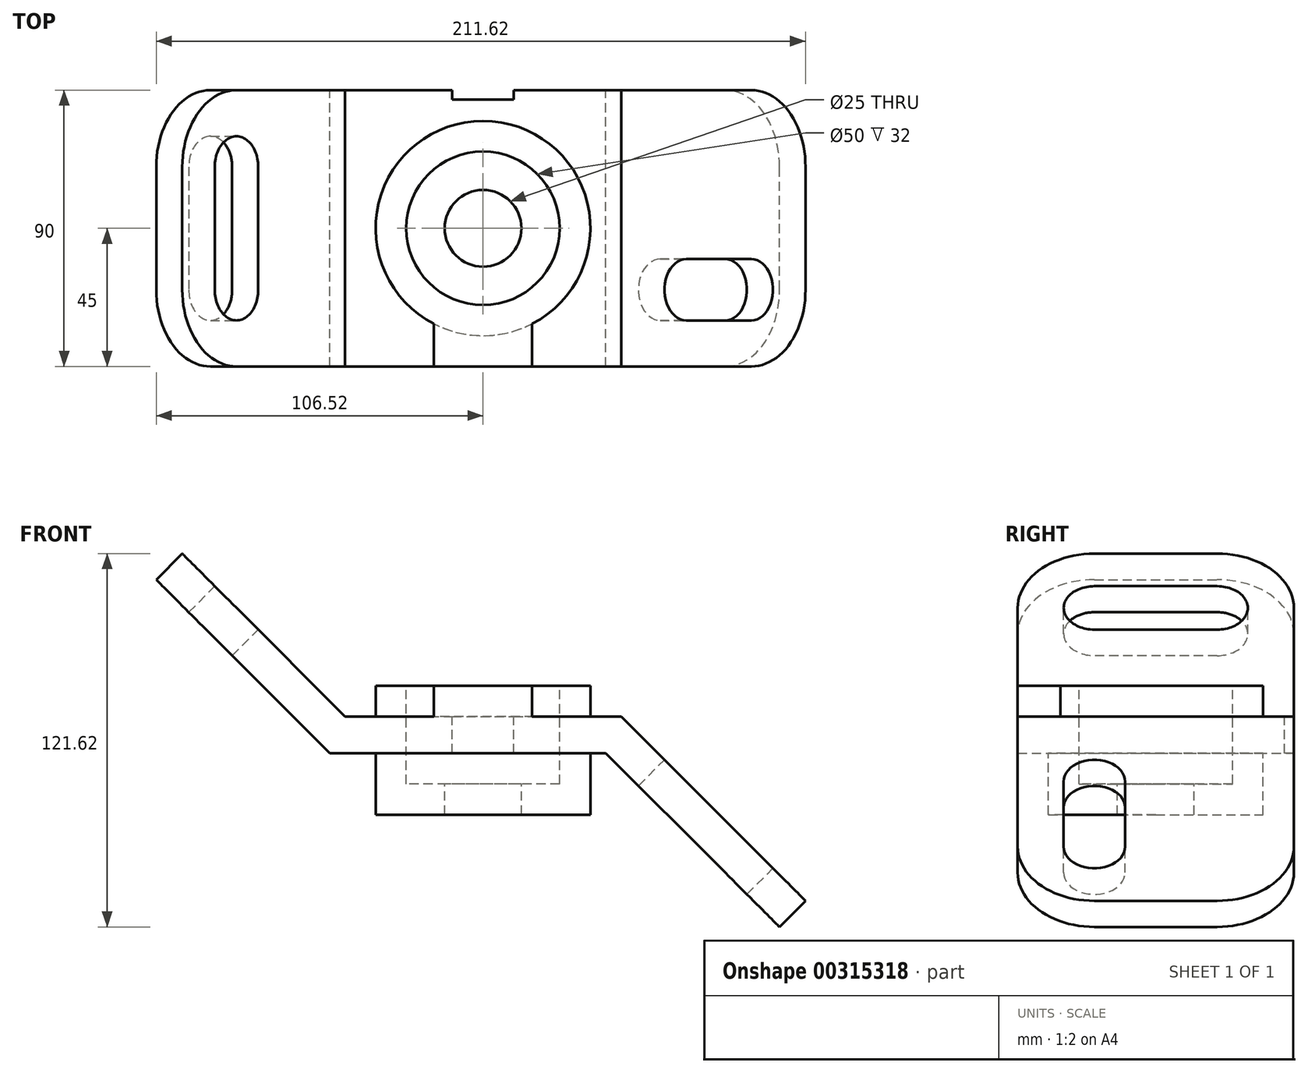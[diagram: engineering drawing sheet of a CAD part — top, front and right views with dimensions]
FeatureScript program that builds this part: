
annotation { "Feature Type Name" : "Feature", "Feature Type Description" : "" }
export const myFeature = defineFeature(function(context is Context, id is Id, definition is map)
    precondition{}
    {
        {
            var Q0;
            Q0=qCreatedBy(makeId("Front.planeOp"),FACE);
            var sketch = newSketch(context, id + "F0", { "sketchPlane" : qUnion([Q0])});
            skLineSegment(sketch, "E0", {"start": v(-98.03, 53.03) * mm, "end": v(-45, 0) * mm});
            skLineSegment(sketch, "E1", {"start": v(-45, 0) * mm, "end": v(45, 0) * mm});
            skLineSegment(sketch, "E2", {"start": v(45, 0) * mm, "end": v(105.1, -60.1) * mm});
            skPoint(sketch, "E3", {"position": v(0, 0) * mm});
            skLineSegment(sketch, "E4.0", {"start": v(40.03, -12) * mm, "end": v(96.62, -68.59) * mm});
            skLineSegment(sketch, "E4.1", {"start": v(-49.97, -12) * mm, "end": v(40.03, -12) * mm});
            skLineSegment(sketch, "E4.2", {"start": v(-106.52, 44.55) * mm, "end": v(-49.97, -12) * mm});
            skLineSegment(sketch, "E5", {"start": v(-106.52, 44.55) * mm, "end": v(-98.03, 53.03) * mm});
            skLineSegment(sketch, "E6", {"start": v(96.62, -68.59) * mm, "end": v(105.1, -60.1) * mm});
            skSolve(sketch);
        }
        {
            var Q0;
            Q0=makeQuery(id+"F0.imprint","IMPRINT",FACE,{"disambiguationData":[TD([[makeQuery(id+"F0.imprint","IMPRINT",EDGE,{"derivedFrom":sQuery(id+"F0.wireOp",EDGE,"E0")}),-1.0]])]});
            extrude(context, id + "F1", {"entities" : qUnion([Q0]), "endBound" : BoundingType.SYMMETRIC, "depth" : 90 * mm});
        }
        {
            var Q0;
            Q0=makeQuery(id+"F1.opExtrude","SWEPT_FACE",FACE,{"disambiguationData":[OSD([sQuery(id+"F0.wireOp",EDGE,"E1")])]});
            var sketch = newSketch(context, id + "F2", { "sketchPlane" : qUnion([Q0])});
            skCircle(sketch, "E7", {"center": v(0, 0) * mm, "radius": 35 * mm});
            skSolve(sketch);
        }
        {
            var Q0;
            Q0=makeQuery(id+"F2.imprint","IMPRINT",FACE,{"disambiguationData":[TD([[makeQuery(id+"F2.imprint","IMPRINT",EDGE,{"derivedFrom":sQuery(id+"F2.wireOp",EDGE,"E7")}),1.0]])]});
            extrude(context, id + "F3", {"entities" : qUnion([Q0]), "operationType" : NewBodyOperationType.ADD, "depth" : 10 * mm});
        }
        {
            var Q0;
            Q0=makeQuery(id+"F1.opExtrude","SWEPT_FACE",FACE,{"disambiguationData":[OSD([sQuery(id+"F0.wireOp",EDGE,"E4.1")])]});
            var sketch = newSketch(context, id + "F4", { "sketchPlane" : qUnion([Q0])});
            skPoint(sketch, "E8.0", {"position": v(0, 0) * mm});
            skCircle(sketch, "E9", {"center": v(0, 0) * mm, "radius": 35 * mm});
            skSolve(sketch);
        }
        {
            var Q0;
            Q0=makeQuery(id+"F4.imprint","IMPRINT",FACE,{"disambiguationData":[TD([[makeQuery(id+"F4.imprint","IMPRINT",EDGE,{"derivedFrom":sQuery(id+"F4.wireOp",EDGE,"E9")}),1.0]])]});
            extrude(context, id + "F5", {"entities" : qUnion([Q0]), "operationType" : NewBodyOperationType.ADD, "depth" : 20 * mm});
        }
        {
            var Q0;
            Q0=makeQuery(id+"F1.opExtrude","CAP_FACE",FACE,{"disambiguationData":[OSD([sQuery(id+"F0.wireOp",EDGE,"E0"),sQuery(id+"F0.wireOp",EDGE,"E1"),sQuery(id+"F0.wireOp",EDGE,"E2"),sQuery(id+"F0.wireOp",EDGE,"E4.0"),sQuery(id+"F0.wireOp",EDGE,"E4.1"),sQuery(id+"F0.wireOp",EDGE,"E4.2"),sQuery(id+"F0.wireOp",EDGE,"E5"),sQuery(id+"F0.wireOp",EDGE,"E6")])],"isStart":false});
            var sketch = newSketch(context, id + "F6", { "sketchPlane" : qUnion([Q0])});
            skPoint(sketch, "E10.0", {"position": v(0, 0) * mm});
            skLineSegment(sketch, "E11.0", {"start": v(-35, 10) * mm, "end": v(35, 10) * mm, "construction": true});
            skLineSegment(sketch, "E12.bottom", {"start": v(0, 0) * mm, "end": v(-16, 0) * mm});
            skLineSegment(sketch, "E12.top", {"start": v(0, 10) * mm, "end": v(-16, 10) * mm});
            skLineSegment(sketch, "E12.left", {"start": v(0, 0) * mm, "end": v(0, 10) * mm, "construction": true});
            skLineSegment(sketch, "E12.right", {"start": v(-16, 0) * mm, "end": v(-16, 10) * mm});
            skLineSegment(sketch, "E13.bottom", {"start": v(0, 0) * mm, "end": v(16, 0) * mm});
            skLineSegment(sketch, "E13.top", {"start": v(0, 10) * mm, "end": v(16, 10) * mm});
            skLineSegment(sketch, "E13.right", {"start": v(16, 0) * mm, "end": v(16, 10) * mm});
            skSolve(sketch);
        }
        {
            var Q0;
            Q0=makeQuery(id+"F6.imprint","IMPRINT",FACE,{"disambiguationData":[TD([[makeQuery(id+"F6.imprint","IMPRINT",EDGE,{"derivedFrom":sQuery(id+"F6.wireOp",EDGE,"E12.bottom")}),1.0]])]});
            var Q1;
            Q1=makeQuery(id+"F1.opExtrude","SWEPT_BODY",BODY,{"disambiguationData":[OSD([sQuery(id+"F0.wireOp",EDGE,"E0"),sQuery(id+"F0.wireOp",EDGE,"E1"),sQuery(id+"F0.wireOp",EDGE,"E2"),sQuery(id+"F0.wireOp",EDGE,"E4.0"),sQuery(id+"F0.wireOp",EDGE,"E4.1"),sQuery(id+"F0.wireOp",EDGE,"E4.2"),sQuery(id+"F0.wireOp",EDGE,"E5"),sQuery(id+"F0.wireOp",EDGE,"E6")])]});
            extrude(context, id + "F7", {"entities" : qUnion([Q0]), "operationType" : NewBodyOperationType.ADD, "endBound" : BoundingType.UP_TO_BODY, "oppositeDirection" : true, "endBoundEntityBody" : qUnion([Q1]), "depth" : 25 * mm});
        }
        {
            var Q0;
            {var subQ0=sQuery(id+"F6.wireOp",EDGE,"E13.top");var subQ1=sQuery(id+"F6.wireOp",EDGE,"E12.top");Q0=makeQuery(id+"F0Bd4dNdUZx9odX_1.1.F7.boolean.opBoolean","MERGE",FACE,{"derivedFrom":[makeQuery(id+"F7.boolean.opBoolean","MERGE",FACE,{"derivedFrom":[makeQuery(id+"F3.opExtrude","CAP_FACE",FACE,{"disambiguationData":[OSD([sQuery(id+"F2.wireOp",EDGE,"E7")])],"isStart":false}),makeQuery(id+"F7.opExtrude","SWEPT_FACE",FACE,{"disambiguationData":[OSD([subQ1,subQ0])]})]}),makeQuery(id+"F0Bd4dNdUZx9odX_1.1.F7.opExtrude","SWEPT_FACE",FACE,{"disambiguationData":[OSD([subQ1,subQ0])]})]});}
            var sketch = newSketch(context, id + "F8", { "sketchPlane" : qUnion([Q0])});
            skPoint(sketch, "E14.0", {"position": v(0, 0) * mm});
            skSolve(sketch);
        }
        {
            var Q0;
            Q0=sQuery(id+"F8.wireOp",VERTEX,"E14.0");
            var Q1;
            Q1=makeQuery(id+"F1.opExtrude","SWEPT_BODY",BODY,{"disambiguationData":[OSD([sQuery(id+"F0.wireOp",EDGE,"E0"),sQuery(id+"F0.wireOp",EDGE,"E1"),sQuery(id+"F0.wireOp",EDGE,"E2"),sQuery(id+"F0.wireOp",EDGE,"E4.0"),sQuery(id+"F0.wireOp",EDGE,"E4.1"),sQuery(id+"F0.wireOp",EDGE,"E4.2"),sQuery(id+"F0.wireOp",EDGE,"E5"),sQuery(id+"F0.wireOp",EDGE,"E6")])]});
            hole(context, id + "F9", {"style" : HoleStyle.C_BORE, "endStyle" : HoleEndStyle.THROUGH, "holeDiameter" : 25 * mm, "cBoreDiameter" : 50 * mm, "cBoreDepth" : 32 * mm, "tappedDepth" : 12 * mm, "tapClearance" : 3, "locations" : qUnion([Q0]), "scope" : qUnion([Q1])});
        }
        {
            var Q0;
            {var subQ0=sQuery(id+"F6.wireOp",EDGE,"E13.top");var subQ1=sQuery(id+"F6.wireOp",EDGE,"E12.top");Q0=makeQuery(id+"F0Bd4dNdUZx9odX_1.1.F7.boolean.opBoolean","MERGE",FACE,{"derivedFrom":[makeQuery(id+"F7.boolean.opBoolean","MERGE",FACE,{"derivedFrom":[makeQuery(id+"F3.opExtrude","CAP_FACE",FACE,{"disambiguationData":[OSD([sQuery(id+"F2.wireOp",EDGE,"E7")])],"isStart":false}),makeQuery(id+"F7.opExtrude","SWEPT_FACE",FACE,{"disambiguationData":[OSD([subQ1,subQ0])]})]}),makeQuery(id+"F0Bd4dNdUZx9odX_1.1.F7.opExtrude","SWEPT_FACE",FACE,{"disambiguationData":[OSD([subQ1,subQ0])]})]});}
            var sketch = newSketch(context, id + "F10", { "sketchPlane" : qUnion([Q0])});
            skPoint(sketch, "E15.0", {"position": v(0, 0) * mm});
            skLineSegment(sketch, "E16", {"start": v(0, 0) * mm, "end": v(0, 59.99) * mm, "construction": true});
            skLineSegment(sketch, "E17.bottom", {"start": v(-10, 45) * mm, "end": v(10, 45) * mm});
            skLineSegment(sketch, "E17.top", {"start": v(-10, 42) * mm, "end": v(10, 42) * mm});
            skLineSegment(sketch, "E17.left", {"start": v(-10, 45) * mm, "end": v(-10, 42) * mm});
            skLineSegment(sketch, "E17.right", {"start": v(10, 45) * mm, "end": v(10, 42) * mm});
            skSolve(sketch);
        }
        {
            var Q0;
            Q0=makeQuery(id+"F10.imprint","IMPRINT",FACE,{"disambiguationData":[TD([[makeQuery(id+"F10.imprint","IMPRINT",EDGE,{"derivedFrom":sQuery(id+"F10.wireOp",EDGE,"E17.bottom")}),-1.0]])]});
            extrude(context, id + "F11", {"entities" : qUnion([Q0]), "operationType" : NewBodyOperationType.REMOVE, "endBound" : BoundingType.THROUGH_ALL, "oppositeDirection" : true, "depth" : 25 * mm});
        }
        {
            var Q0;
            Q0=makeQuery(id+"F1.opExtrude","CAP_EDGE",EDGE,{"disambiguationData":[OSD([sQuery(id+"F0.wireOp",EDGE,"E5")])],"isStart":false});
            var Q1;
            Q1=makeQuery(id+"F1.opExtrude","CAP_EDGE",EDGE,{"disambiguationData":[OSD([sQuery(id+"F0.wireOp",EDGE,"E5")])],"isStart":true});
            var Q2;
            Q2=makeQuery(id+"F1.opExtrude","CAP_EDGE",EDGE,{"disambiguationData":[OSD([sQuery(id+"F0.wireOp",EDGE,"E6")])],"isStart":false});
            var Q3;
            Q3=makeQuery(id+"F1.opExtrude","CAP_EDGE",EDGE,{"disambiguationData":[OSD([sQuery(id+"F0.wireOp",EDGE,"E6")])],"isStart":true});
            fillet(context, id + "F12", {"entities" : qUnion([Q0, Q1, Q2, Q3]), "radius" : 25 * mm, "tangentPropagation" : true, "allowEdgeOverflow" : false});
        }
        {
            var Q0;
            Q0=makeQuery(id+"F1.opExtrude","SWEPT_FACE",FACE,{"disambiguationData":[OSD([sQuery(id+"F0.wireOp",EDGE,"E0")])]});
            var sketch = newSketch(context, id + "F13", { "sketchPlane" : qUnion([Q0])});
            skArc(sketch, "E18.0", {"start": v(-20, 106.82) * mm, "mid": v(-37.68, 99.5) * mm, "end": v(-45, 81.82) * mm});
            skArc(sketch, "E19.0", {"start": v(45, 81.82) * mm, "mid": v(37.68, 99.5) * mm, "end": v(20, 106.82) * mm});
            skArc(sketch, "E20", {"start": v(-20, 91.82) * mm, "mid": v(-30, 81.82) * mm, "end": v(-20, 71.82) * mm});
            skArc(sketch, "E21", {"start": v(20, 71.82) * mm, "mid": v(30, 81.82) * mm, "end": v(20, 91.82) * mm});
            skLineSegment(sketch, "E22", {"start": v(-20, 91.82) * mm, "end": v(20, 91.82) * mm});
            skLineSegment(sketch, "E23", {"start": v(-20, 71.82) * mm, "end": v(20, 71.82) * mm});
            skSolve(sketch);
        }
        {
            var Q0;
            Q0=makeQuery(id+"F13.imprint","IMPRINT",FACE,{"disambiguationData":[TD([[makeQuery(id+"F13.imprint","IMPRINT",EDGE,{"derivedFrom":sQuery(id+"F13.wireOp",EDGE,"E20")}),1.0]])]});
            extrude(context, id + "F14", {"entities" : qUnion([Q0]), "operationType" : NewBodyOperationType.REMOVE, "endBound" : BoundingType.UP_TO_NEXT, "oppositeDirection" : true, "depth" : 25 * mm});
        }
        {
            var Q0;
            Q0=makeQuery(id+"F1.opExtrude","SWEPT_FACE",FACE,{"disambiguationData":[OSD([sQuery(id+"F0.wireOp",EDGE,"E2")])]});
            var sketch = newSketch(context, id + "F15", { "sketchPlane" : qUnion([Q0])});
            skArc(sketch, "E24.0", {"start": v(-45, -91.82) * mm, "mid": v(-37.68, -109.5) * mm, "end": v(-20, -116.82) * mm});
            skArc(sketch, "E25", {"start": v(-30, -91.82) * mm, "mid": v(-20, -101.82) * mm, "end": v(-10, -91.82) * mm});
            skArc(sketch, "E26", {"start": v(-10, -61.82) * mm, "mid": v(-20, -51.82) * mm, "end": v(-30, -61.82) * mm});
            skLineSegment(sketch, "E27", {"start": v(-30, -61.82) * mm, "end": v(-30, -91.82) * mm});
            skLineSegment(sketch, "E28", {"start": v(-10, -61.82) * mm, "end": v(-10, -91.82) * mm});
            skSolve(sketch);
        }
        {
            var Q0;
            Q0=makeQuery(id+"F15.imprint","IMPRINT",FACE,{"disambiguationData":[TD([[makeQuery(id+"F15.imprint","IMPRINT",EDGE,{"derivedFrom":sQuery(id+"F15.wireOp",EDGE,"E25")}),1.0]])]});
            extrude(context, id + "F16", {"entities" : qUnion([Q0]), "operationType" : NewBodyOperationType.REMOVE, "endBound" : BoundingType.UP_TO_NEXT, "oppositeDirection" : true, "depth" : 25 * mm});
        }
    });
